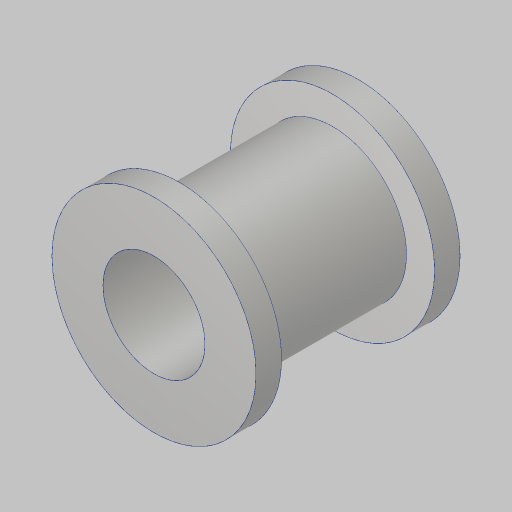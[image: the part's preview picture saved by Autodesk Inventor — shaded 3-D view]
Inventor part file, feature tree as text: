
AUTODESK INVENTOR PART (.ipt)
format: ipt  version: 2023.5 (Build 275446000, 446)  size: 153,088 bytes
history: native  units: in
note: dims shown in document units (in); Inventor stores cm internally (conversion verified against a paired STEP export)
features: extrude x3, sketch x3, projected_geometry x2
ambient origin geometry x8: Origin, YZ Plane, XZ Plane, XY Plane, X Axis, Y Axis, Z Axis, Center Point
bodies: Solid1 (feature_tree)
feature tree (8):
  extrude  "Extrusion1"  Depth=1.0in
  extrude  "Extrusion2"  Depth=1.0in
  extrude  "Extrusion3"  Depth=0.5in
  sketch  "Sketch1"  dims[d1=1.0in d2=6.0in]
  sketch  "Sketch2"  dims[d3=1.0in d4=6.0in]
  projected_geometry  "Projected Loop1"
  sketch  "Sketch3"  dims[d5=0.25in d6=0.5in d7=0.0625in d8=0.015in d11=0.725in d12=0.75in d13=0.0in d15=0.125in d16=0.0in d18=0.125in d19=0.0in d21=0.3475in d22=1.0in d23=1.0in d24=0.5in d25=0.0344in d26=0.5in d27=0.0344in]
  projected_geometry  "Projected Loop2"
